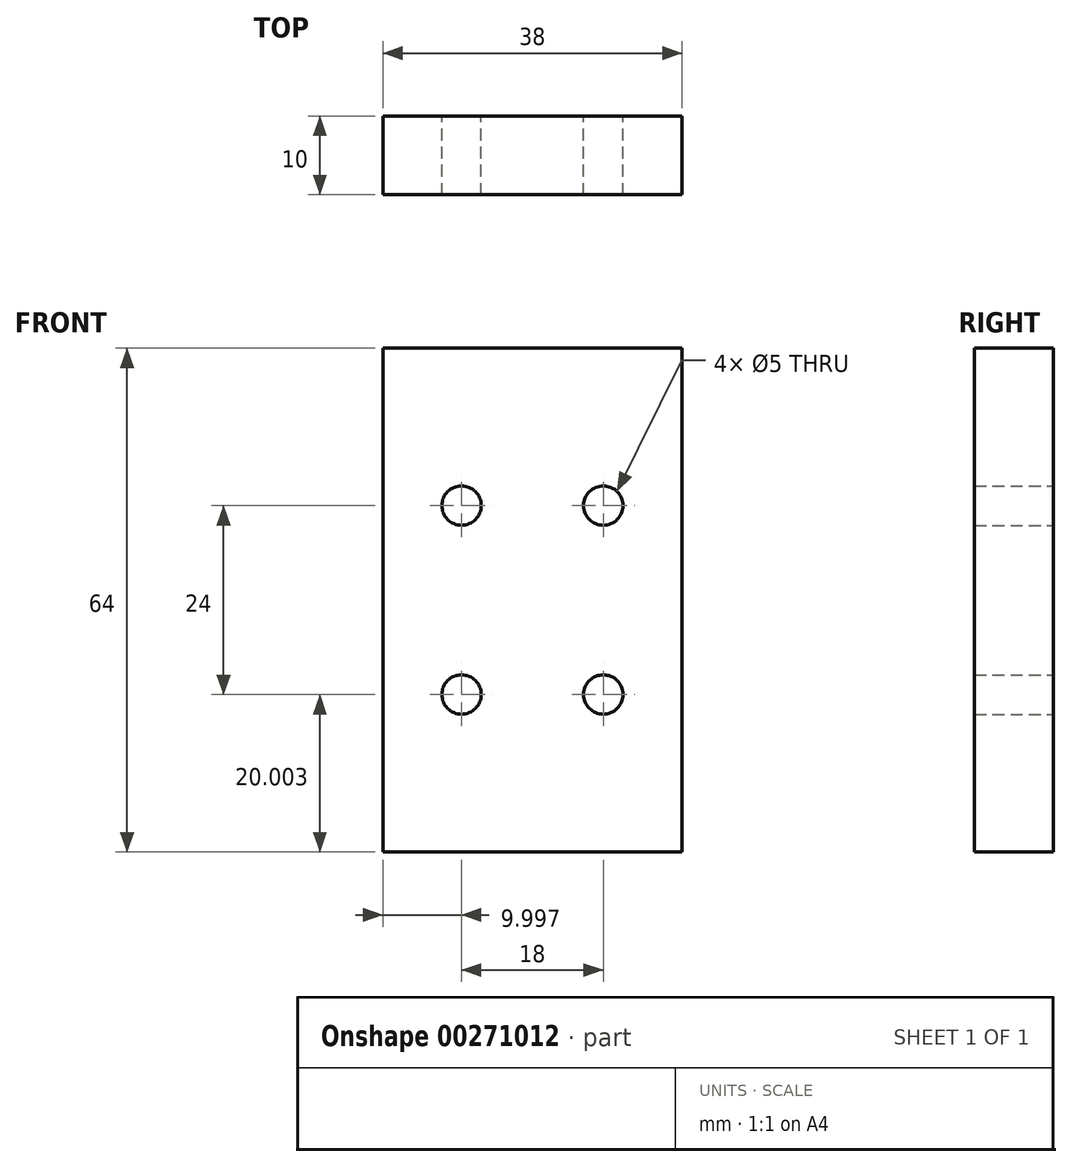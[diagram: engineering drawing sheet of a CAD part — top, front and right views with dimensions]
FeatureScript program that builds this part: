
annotation { "Feature Type Name" : "Feature", "Feature Type Description" : "" }
export const myFeature = defineFeature(function(context is Context, id is Id, definition is map)
    precondition{}
    {
        {
            var Q0;
            Q0=qCreatedBy(makeId("Front.planeOp"),FACE);
            var sketch = newSketch(context, id + "F0", { "sketchPlane" : qUnion([Q0])});
            skLineSegment(sketch, "E0.bottom", {"start": v(-18.56, 28.31) * mm, "end": v(19.44, 28.31) * mm});
            skLineSegment(sketch, "E0.top", {"start": v(-18.56, -35.69) * mm, "end": v(19.44, -35.69) * mm});
            skLineSegment(sketch, "E0.left", {"start": v(-18.56, 28.31) * mm, "end": v(-18.56, -35.69) * mm});
            skLineSegment(sketch, "E0.right", {"start": v(19.44, 28.31) * mm, "end": v(19.44, -35.69) * mm});
            skLineSegment(sketch, "E1.bottom", {"start": v(-8.56, 8.31) * mm, "end": v(9.44, 8.31) * mm});
            skLineSegment(sketch, "E1.top", {"start": v(-8.56, -15.69) * mm, "end": v(9.44, -15.69) * mm});
            skLineSegment(sketch, "E1.left", {"start": v(-8.56, 8.31) * mm, "end": v(-8.56, -15.69) * mm});
            skLineSegment(sketch, "E1.right", {"start": v(9.44, 8.31) * mm, "end": v(9.44, -15.69) * mm});
            skCircle(sketch, "E2", {"center": v(-8.56, 8.31) * mm, "radius": 2.5 * mm});
            skCircle(sketch, "E3", {"center": v(9.44, 8.31) * mm, "radius": 2.5 * mm});
            skCircle(sketch, "E4", {"center": v(9.44, -15.69) * mm, "radius": 2.5 * mm});
            skCircle(sketch, "E5", {"center": v(-8.56, -15.69) * mm, "radius": 2.5 * mm});
            skSolve(sketch);
        }
        {
            var Q0;
            Q0 = qSketchRegion(id + "F0", true);
            var Q1;
            {var subQ5=sQuery(id+"F0.wireOp",EDGE,"E1.bottom");var subQ7=sQuery(id+"F0.wireOp",EDGE,"E2");var subQ15=makeQuery(id+"F0.imprint","INTERSECT",VERTEX,{"derivedFrom":[subQ5,subQ7]});Q1=makeQuery(id+"F0.imprint","IMPRINT",FACE,{"disambiguationData":[TD([[makeQuery(id+"F0.imprint","IMPRINT",EDGE,{"disambiguationData":[TD([[subQ15,-1.0]])],"derivedFrom":subQ5}),-1.0]])]});}
            extrude(context, id + "F1", {"entities" : qUnion([Q0, Q1]), "depth" : 10 * mm});
        }
    });
